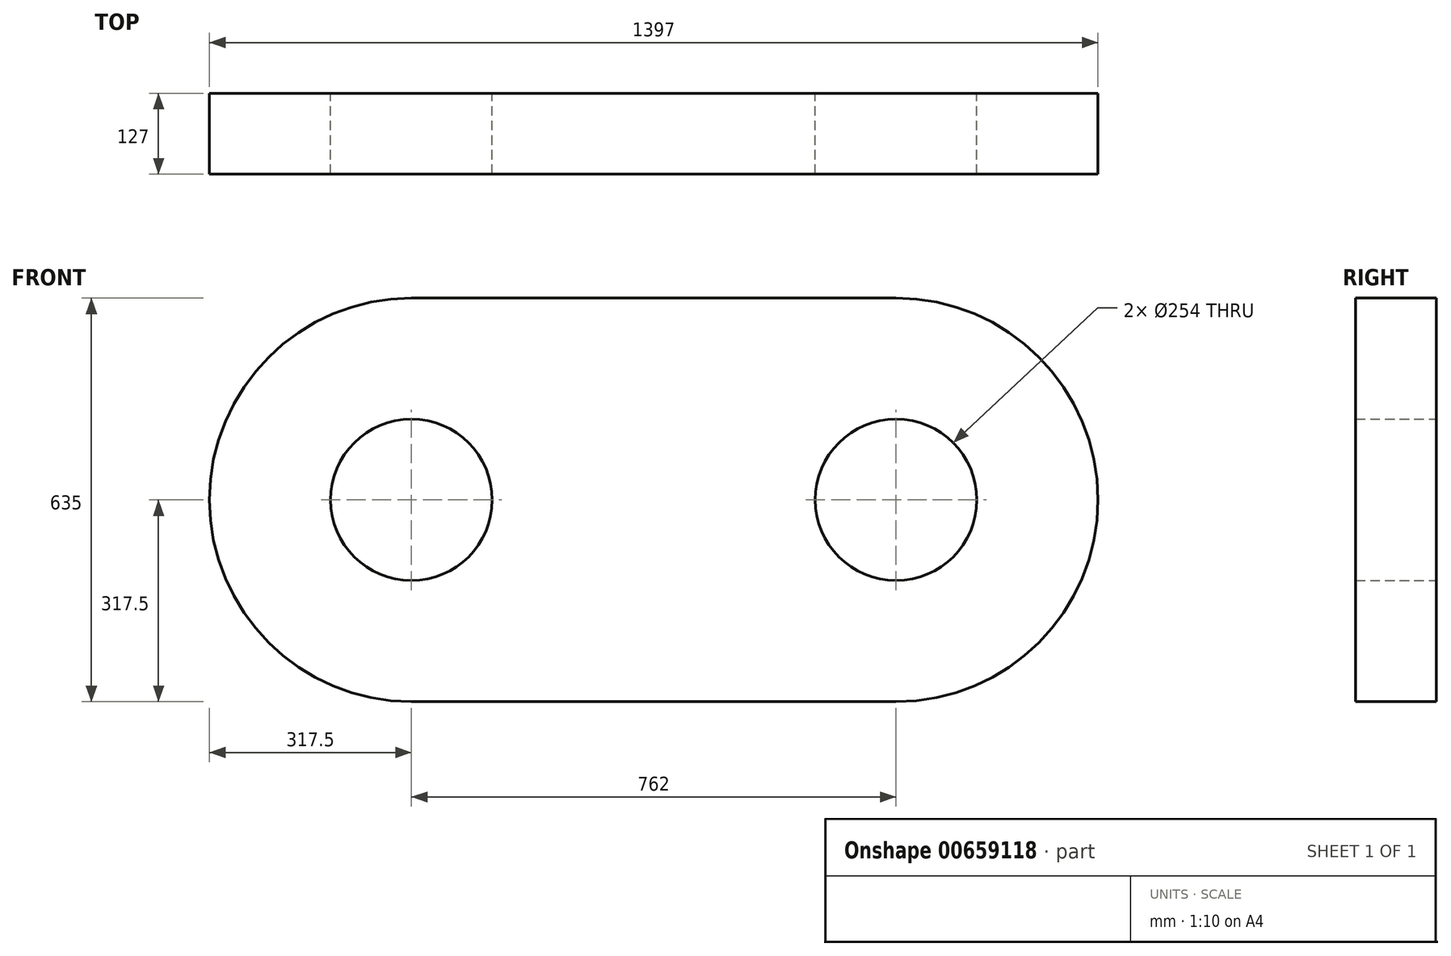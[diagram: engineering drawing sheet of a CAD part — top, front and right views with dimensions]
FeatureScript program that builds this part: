
annotation { "Feature Type Name" : "Feature", "Feature Type Description" : "" }
export const myFeature = defineFeature(function(context is Context, id is Id, definition is map)
    precondition{}
    {
        {
            var Q0;
            Q0=qCreatedBy(makeId("Front.planeOp"),FACE);
            var sketch = newSketch(context, id + "F0", { "sketchPlane" : qUnion([Q0])});
            skLineSegment(sketch, "E0.bottom", {"start": v(-381, 317.5) * mm, "end": v(381, 317.5) * mm});
            skLineSegment(sketch, "E0.top", {"start": v(-381, -317.5) * mm, "end": v(381, -317.5) * mm});
            skArc(sketch, "E1", {"start": v(381, -317.5) * mm, "mid": v(698.5, 0) * mm, "end": v(381, 317.5) * mm});
            skArc(sketch, "E2", {"start": v(-381, 317.5) * mm, "mid": v(-698.5, 0) * mm, "end": v(-381, -317.5) * mm});
            skCircle(sketch, "E3", {"center": v(-381, 0) * mm, "radius": 127 * mm});
            skCircle(sketch, "E4", {"center": v(381, 0) * mm, "radius": 127 * mm});
            skSolve(sketch);
        }
        {
            var Q0;
            Q0 = qSketchRegion(id + "F0", true);
            extrude(context, id + "F1", {"entities" : qUnion([Q0]), "endBound" : BoundingType.SYMMETRIC, "depth" : 127 * mm, "offsetDistance" : 25.4 * mm});
        }
    });
